# Revit family: AVP Actuator_Flow_PN16_RFA
name_source: partatom
category: Pipe Accessories
units: mm (PartAtom-declared; Revit-internal decimal feet)

## family parameters
Always vertical = Yes
Cut with Voids When Loaded = No
OmniClass Number = 23.65.55.14.17
OmniClass Title = Adjusting/Controlling Valves for Liquid Services
Part Type = Normal
Round Connector Dimension = Use Diameter
Shared = No
Work Plane-Based = No

## types (2) — shared parameters
Actuator size = 39.0 cm²
Body Material = Danfoss Steel Zinc Plated
Description = Spring Actuator
Manufacturer = Danfoss
Nominal Pressure = PN 16
URL = https://store.danfoss.com

## per-type parameters (varying)
| type | Differential Pressure Setting Range | Model | Model Type | Spring Colour |
| AVP Actuator_Flow_PN16_dP0.05-0.5bar_003H6823 | 0.05-0.5 bar | 003H6823 | AVP Actuator_Flow_PN16_dP0.05-0.5bar | Danfoss Steel Paint Grey (Spring) |
| AVP Actuator_Flow_PN16_dP0.2-1.0/0.8-1.6 bar_003H6824 | 0.2-1.0 bar / 0.8-1.6 bar | 003H6824 | AVP Actuator_Flow_PN16_dP0.2-1.0/0.8-1.6 bar | Danfoss Steel Paint Black (Spring) |

## geometry (parser evidence)
native form markers: Sweep x3
no freeform markers — native parametric forms only
